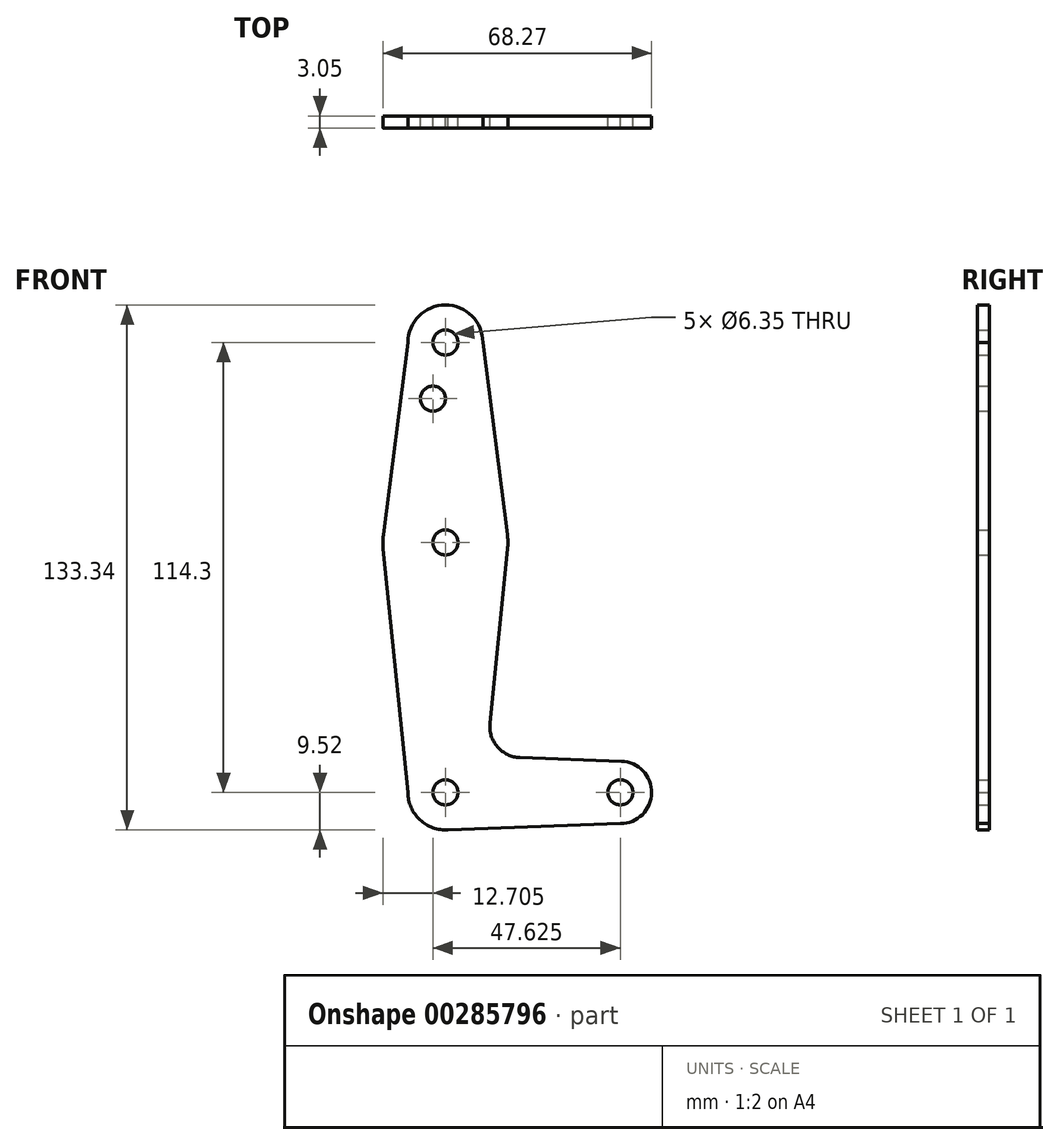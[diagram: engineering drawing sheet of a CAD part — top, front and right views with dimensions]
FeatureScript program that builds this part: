
annotation { "Feature Type Name" : "Feature", "Feature Type Description" : "" }
export const myFeature = defineFeature(function(context is Context, id is Id, definition is map)
    precondition{}
    {
        {
            var Q0;
            Q0=qCreatedBy(makeId("Front.planeOp"),FACE);
            var sketch = newSketch(context, id + "F0", { "sketchPlane" : qUnion([Q0])});
            skLineSegment(sketch, "E0", {"start": v(0, 50.8) * mm, "end": v(0, -63.5) * mm, "construction": true});
            skLineSegment(sketch, "E1", {"start": v(0, -63.5) * mm, "end": v(44.45, -63.5) * mm, "construction": true});
            skCircle(sketch, "E2", {"center": v(0, 50.8) * mm, "radius": 9.53 * mm});
            skCircle(sketch, "E3", {"center": v(0, 0) * mm, "radius": 15.88 * mm});
            skCircle(sketch, "E4", {"center": v(0, -63.5) * mm, "radius": 9.53 * mm});
            skCircle(sketch, "E5", {"center": v(44.45, -63.5) * mm, "radius": 7.94 * mm});
            skLineSegment(sketch, "E6", {"start": v(-9.52, 50.8) * mm, "end": v(-15.75, 2) * mm});
            skLineSegment(sketch, "E7", {"start": v(0, -73.02) * mm, "end": v(44.45, -71.44) * mm});
            skLineSegment(sketch, "E8", {"start": v(9.53, 50.8) * mm, "end": v(15.75, 2) * mm});
            skLineSegment(sketch, "E9", {"start": v(18.93, -54.65) * mm, "end": v(44.73, -55.57) * mm});
            skLineSegment(sketch, "E10", {"start": v(-9.52, -63.5) * mm, "end": v(-15.8, -1.6) * mm});
            skLineSegment(sketch, "E11", {"start": v(11.3, -45.9) * mm, "end": v(15.8, -1.6) * mm});
            skCircle(sketch, "E12", {"center": v(0, 50.8) * mm, "radius": 3.18 * mm});
            skCircle(sketch, "E13", {"center": v(0, 0) * mm, "radius": 3.18 * mm});
            skCircle(sketch, "E14", {"center": v(0, -63.5) * mm, "radius": 3.18 * mm});
            skCircle(sketch, "E15", {"center": v(44.45, -63.5) * mm, "radius": 3.18 * mm});
            skPoint(sketch, "E16.newPointA", {"position": v(0, -53.98) * mm});
            skArc(sketch, "E16.filletArc", {"start": v(11.3, -45.9) * mm, "mid": v(13.22, -51.93) * mm, "end": v(18.93, -54.65) * mm});
            skPoint(sketch, "E17.centerSnap0", {"position": v(12.64, 26.4) * mm});
            skCircle(sketch, "E18", {"center": v(-3.17, 36.53) * mm, "radius": 3.18 * mm});
            skSolve(sketch);
        }
        {
            var Q0;
            Q0 = qSketchRegion(id + "F0", true);
            extrude(context, id + "F1", {"entities" : qUnion([Q0]), "depth" : 3.05 * mm});
        }
    });
